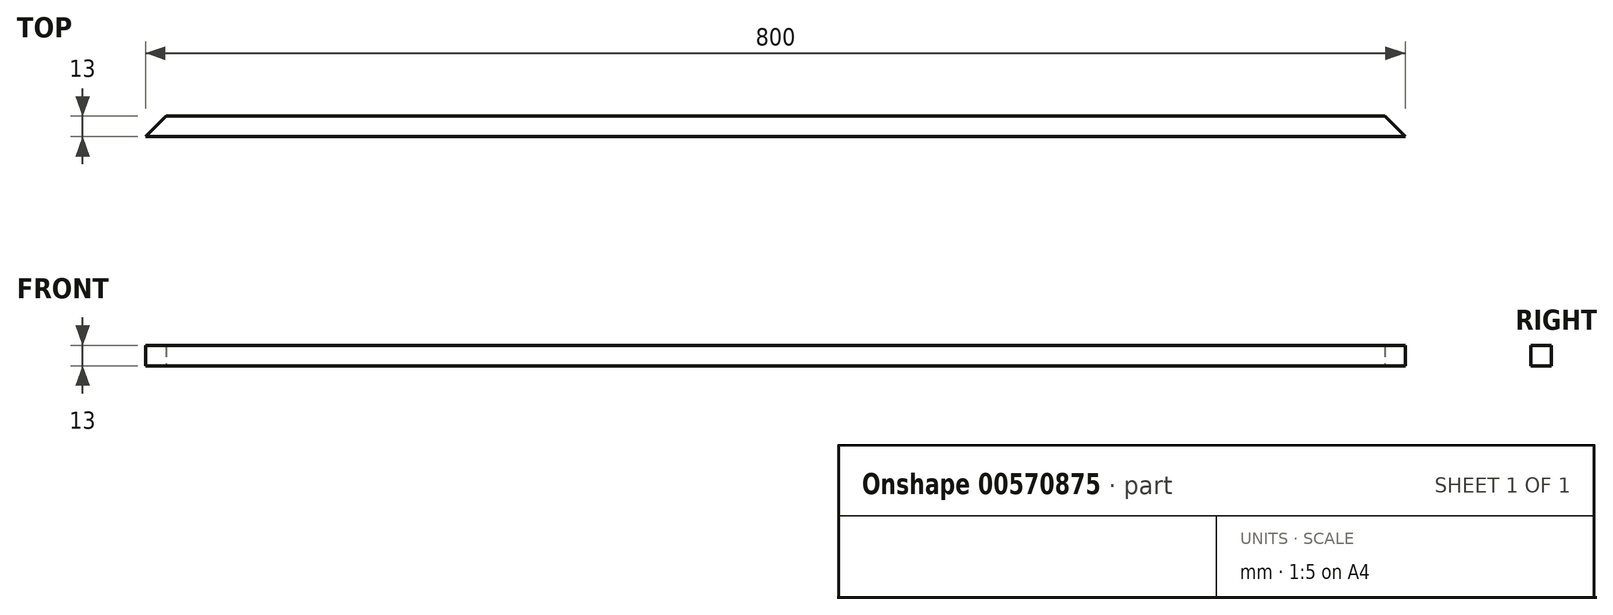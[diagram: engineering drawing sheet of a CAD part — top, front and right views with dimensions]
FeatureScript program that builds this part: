
annotation { "Feature Type Name" : "Feature", "Feature Type Description" : "" }
export const myFeature = defineFeature(function(context is Context, id is Id, definition is map)
    precondition{}
    {
        {
            var Q0;
            Q0=qCreatedBy(makeId("Top.planeOp"),FACE);
            var sketch = newSketch(context, id + "F0", { "sketchPlane" : qUnion([Q0])});
            skLineSegment(sketch, "E0.bottom", {"start": v(-400, 0) * mm, "end": v(400, 0) * mm});
            skLineSegment(sketch, "E0.top", {"start": v(-387, 13) * mm, "end": v(387, 13) * mm});
            skLineSegment(sketch, "E1", {"start": v(-400, 0) * mm, "end": v(-387, 13) * mm});
            skLineSegment(sketch, "E2", {"start": v(400, 0) * mm, "end": v(387, 13) * mm});
            skSolve(sketch);
        }
        {
            var Q0;
            Q0=makeQuery(id+"F0.imprint","IMPRINT",FACE,{"disambiguationData":[TD([[makeQuery(id+"F0.imprint","IMPRINT",EDGE,{"derivedFrom":sQuery(id+"F0.wireOp",EDGE,"E0.bottom")}),1.0]])]});
            extrude(context, id + "F1", {"entities" : qUnion([Q0]), "depth" : 13 * mm, "offsetDistance" : 25 * mm});
        }
    });
